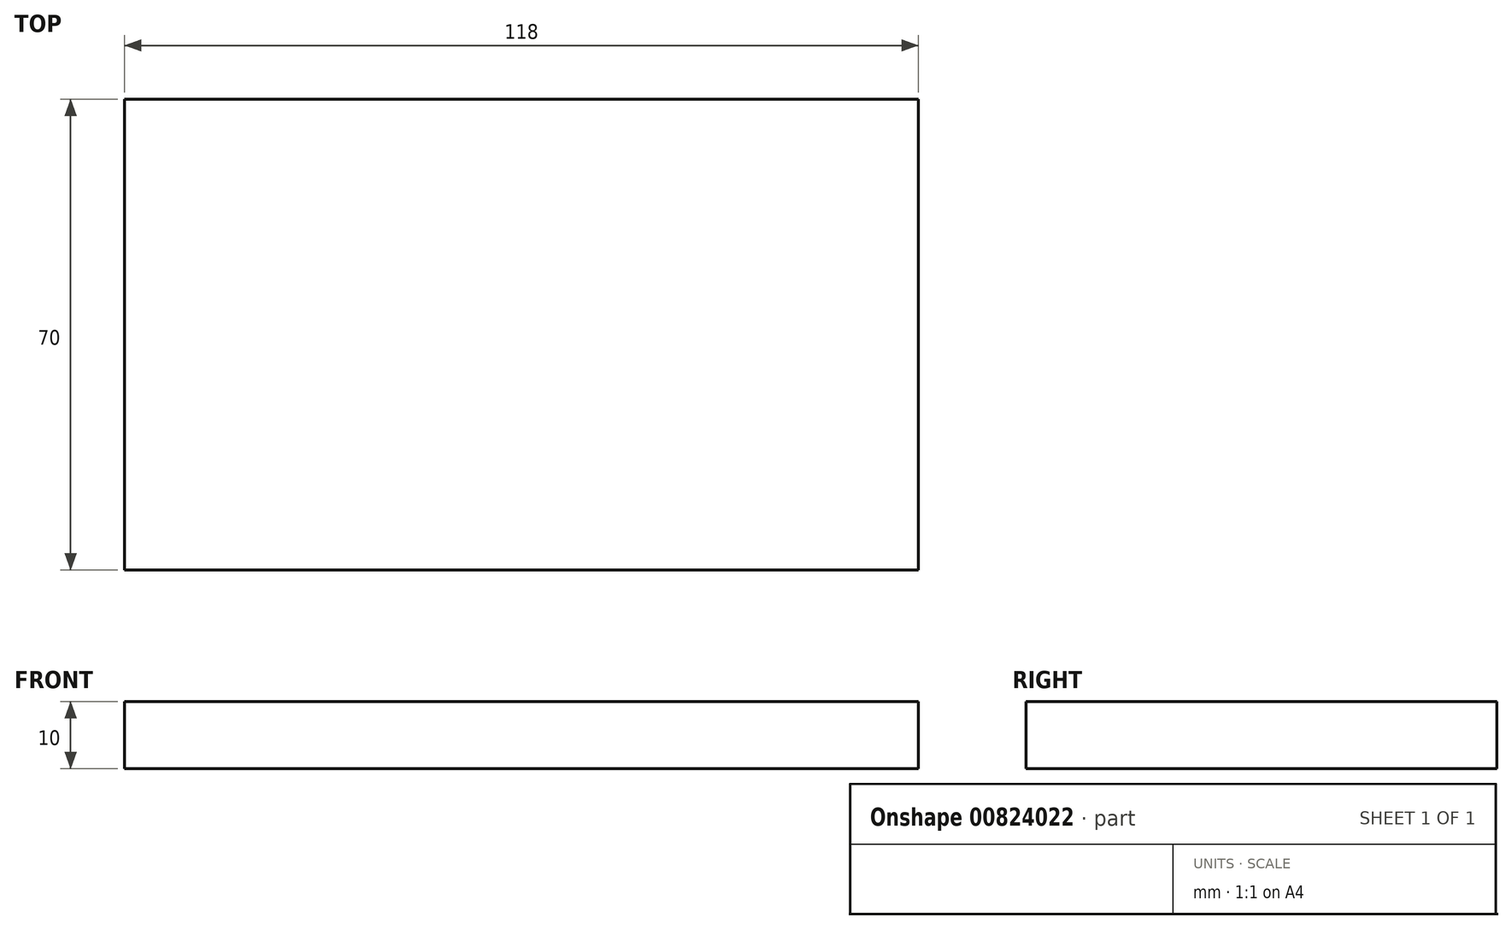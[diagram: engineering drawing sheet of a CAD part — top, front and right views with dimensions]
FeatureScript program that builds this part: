
annotation { "Feature Type Name" : "Feature", "Feature Type Description" : "" }
export const myFeature = defineFeature(function(context is Context, id is Id, definition is map)
    precondition{}
    {
        {
            var Q0;
            Q0=qCreatedBy(makeId("Front.planeOp"),FACE);
            var sketch = newSketch(context, id + "F0", { "sketchPlane" : qUnion([Q0])});
            skLineSegment(sketch, "E0.bottom", {"start": v(59, 5) * mm, "end": v(-59, 5) * mm});
            skLineSegment(sketch, "E0.top", {"start": v(59, -5) * mm, "end": v(-59, -5) * mm});
            skLineSegment(sketch, "E0.left", {"start": v(59, 5) * mm, "end": v(59, -5) * mm});
            skLineSegment(sketch, "E0.right", {"start": v(-59, 5) * mm, "end": v(-59, -5) * mm});
            skPoint(sketch, "E0.middle", {"position": v(0, 0) * mm});
            skSolve(sketch);
        }
        {
            var Q0;
            Q0 = qSketchRegion(id + "F0", true);
            extrude(context, id + "F1", {"entities" : qUnion([Q0]), "endBound" : BoundingType.SYMMETRIC, "depth" : 70 * mm, "offsetDistance" : 25 * mm});
        }
    });
